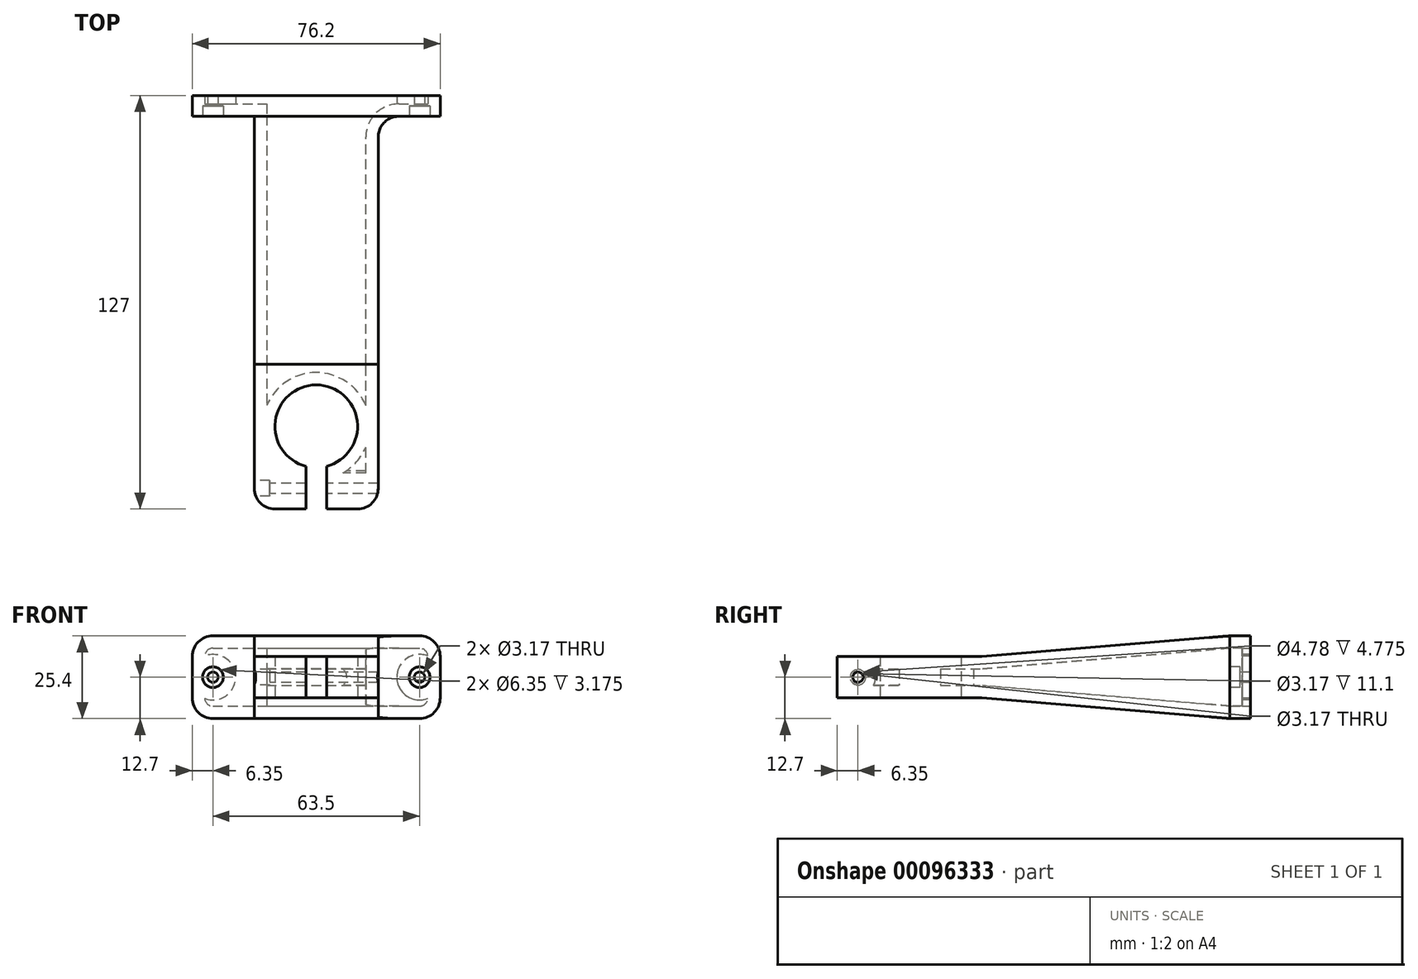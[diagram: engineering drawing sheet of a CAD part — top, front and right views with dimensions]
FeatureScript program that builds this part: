
annotation { "Feature Type Name" : "Feature", "Feature Type Description" : "" }
export const myFeature = defineFeature(function(context is Context, id is Id, definition is map)
    precondition{}
    {
        {
            var Q0;
            Q0=qCreatedBy(makeId("Front.planeOp"),FACE);
            var sketch = newSketch(context, id + "F0", { "sketchPlane" : qUnion([Q0])});
            skLineSegment(sketch, "E0.bottom", {"start": v(0, 0) * mm, "end": v(76.2, 0) * mm});
            skLineSegment(sketch, "E0.top", {"start": v(0, 25.4) * mm, "end": v(76.2, 25.4) * mm});
            skLineSegment(sketch, "E0.left", {"start": v(0, 0) * mm, "end": v(0, 25.4) * mm});
            skLineSegment(sketch, "E0.right", {"start": v(76.2, 0) * mm, "end": v(76.2, 25.4) * mm});
            skSolve(sketch);
        }
        {
            var Q0;
            Q0=makeQuery(id+"F0.imprint","IMPRINT",FACE,{"disambiguationData":[TD([[makeQuery(id+"F0.imprint","IMPRINT",EDGE,{"derivedFrom":sQuery(id+"F0.wireOp",EDGE,"E0.bottom")}),1.0]])]});
            extrude(context, id + "F1", {"entities" : qUnion([Q0]), "depth" : 6.35 * mm});
        }
        {
            var Q0;
            Q0=makeQuery(id+"F1.opExtrude","CAP_FACE",FACE,{"disambiguationData":[OSD([sQuery(id+"F0.wireOp",EDGE,"E0.bottom"),sQuery(id+"F0.wireOp",EDGE,"E0.top"),sQuery(id+"F0.wireOp",EDGE,"E0.left"),sQuery(id+"F0.wireOp",EDGE,"E0.right")])],"isStart":false});
            var sketch = newSketch(context, id + "F2", { "sketchPlane" : qUnion([Q0])});
            skPoint(sketch, "E1", {"position": v(6.35, 12.7) * mm});
            skPoint(sketch, "E1.positionSnap0", {"position": v(0, 12.7) * mm});
            skPoint(sketch, "E2", {"position": v(76.2, 12.7) * mm});
            skPoint(sketch, "E3", {"position": v(69.85, 12.7) * mm});
            skSolve(sketch);
        }
        {
            var Q0;
            Q0=sQuery(id+"F2.wireOp",VERTEX,"E1");
            var Q1;
            Q1=sQuery(id+"F2.wireOp",VERTEX,"E3");
            var Q2;
            Q2=makeQuery(id+"F1.opExtrude","SWEPT_BODY",BODY,{"disambiguationData":[OSD([sQuery(id+"F0.wireOp",EDGE,"E0.bottom"),sQuery(id+"F0.wireOp",EDGE,"E0.top"),sQuery(id+"F0.wireOp",EDGE,"E0.left"),sQuery(id+"F0.wireOp",EDGE,"E0.right")])]});
            hole(context, id + "F3", {"style" : HoleStyle.C_BORE, "endStyle" : HoleEndStyle.THROUGH, "holeDiameter" : 3.17 * mm, "cBoreDiameter" : 6.35 * mm, "cBoreDepth" : 3.17 * mm, "locations" : qUnion([Q0, Q1]), "scope" : qUnion([Q2]), "isTappedThrough" : true});
        }
        {
            var Q0;
            Q0=makeQuery(id+"F1.opExtrude","CAP_FACE",FACE,{"disambiguationData":[OSD([sQuery(id+"F0.wireOp",EDGE,"E0.bottom"),sQuery(id+"F0.wireOp",EDGE,"E0.top"),sQuery(id+"F0.wireOp",EDGE,"E0.left"),sQuery(id+"F0.wireOp",EDGE,"E0.right")])],"isStart":false});
            var sketch = newSketch(context, id + "F4", { "sketchPlane" : qUnion([Q0])});
            skLineSegment(sketch, "E4.bottom", {"start": v(19.05, 25.4) * mm, "end": v(57.15, 25.4) * mm});
            skLineSegment(sketch, "E4.top", {"start": v(19.05, 0) * mm, "end": v(57.15, 0) * mm});
            skLineSegment(sketch, "E4.left", {"start": v(19.05, 25.4) * mm, "end": v(19.05, 0) * mm});
            skLineSegment(sketch, "E4.right", {"start": v(57.15, 25.4) * mm, "end": v(57.15, 0) * mm});
            skSolve(sketch);
        }
        {
            var Q0;
            Q0=makeQuery(id+"F4.imprint","IMPRINT",FACE,{"disambiguationData":[TD([[makeQuery(id+"F4.imprint","IMPRINT",EDGE,{"derivedFrom":sQuery(id+"F4.wireOp",EDGE,"E4.bottom")}),-1.0]])]});
            cPlane(context, id + "F5", {"entities" : qUnion([Q0]), "cplaneType" : CPlaneType.OFFSET, "offset" : 76.2 * mm, "width" : 152.4 * mm, "height" : 152.4 * mm});
        }
        {
            var Q0;
            Q0=qCreatedBy(id+"F5.planeOp",FACE);
            var sketch = newSketch(context, id + "F6", { "sketchPlane" : qUnion([Q0])});
            skLineSegment(sketch, "E5.0", {"start": v(19.05, 25.4) * mm, "end": v(57.15, 25.4) * mm, "construction": true});
            skLineSegment(sketch, "E6.0", {"start": v(19.05, 0) * mm, "end": v(57.15, 0) * mm, "construction": true});
            skLineSegment(sketch, "E7.0", {"start": v(19.05, 25.4) * mm, "end": v(19.05, 0) * mm, "construction": true});
            skLineSegment(sketch, "E8.0", {"start": v(57.15, 25.4) * mm, "end": v(57.15, 0) * mm, "construction": true});
            skLineSegment(sketch, "E9.bottom", {"start": v(19.05, 19.05) * mm, "end": v(57.15, 19.05) * mm});
            skLineSegment(sketch, "E9.top", {"start": v(19.05, 6.35) * mm, "end": v(57.15, 6.35) * mm});
            skLineSegment(sketch, "E9.left", {"start": v(19.05, 19.05) * mm, "end": v(19.05, 6.35) * mm});
            skLineSegment(sketch, "E9.right", {"start": v(57.15, 19.05) * mm, "end": v(57.15, 6.35) * mm});
            skSolve(sketch);
        }
        {
            var Q1;
            Q1=makeQuery(id+"F6.imprint","IMPRINT",FACE,{"disambiguationData":[TD([[makeQuery(id+"F6.imprint","IMPRINT",EDGE,{"derivedFrom":sQuery(id+"F6.wireOp",EDGE,"E9.bottom")}),-1.0]])]});
            var Q2;
            Q2=makeQuery(id+"F4.imprint","IMPRINT",FACE,{"disambiguationData":[TD([[makeQuery(id+"F4.imprint","IMPRINT",EDGE,{"derivedFrom":sQuery(id+"F4.wireOp",EDGE,"E4.bottom")}),-1.0]])]});
            loft(context, id + "F7", {"operationType" : NewBodyOperationType.ADD, "sheetProfilesArray" : [{ "sheetProfileEntities" : qUnion([Q1]) }, { "sheetProfileEntities" : qUnion([Q2]) }]});
        }
        {
            var Q0;
            Q0=makeQuery(id+"F7.opLoft","CAP_FACE",FACE,{"disambiguationData":[OSD([makeQuery(id+"F6.imprint","IMPRINT",FACE,{"disambiguationData":[TD([[makeQuery(id+"F6.imprint","IMPRINT",EDGE,{"derivedFrom":sQuery(id+"F6.wireOp",EDGE,"E9.bottom")}),-1.0]])]})])],"isStart":true});
            extrude(context, id + "F8", {"entities" : qUnion([Q0]), "operationType" : NewBodyOperationType.ADD, "depth" : 38.1 * mm});
        }
        {
            var Q0;
            Q0=makeQuery(id+"F8.opExtrude","SWEPT_FACE",FACE,{"disambiguationData":[OSD([sQuery(id+"F6.wireOp",EDGE,"E9.top"),sQuery(id+"F6.wireOp",EDGE,"E9.left"),sQuery(id+"F6.wireOp",EDGE,"E9.right")])]});
            var sketch = newSketch(context, id + "F9", { "sketchPlane" : qUnion([Q0])});
            skPoint(sketch, "E10", {"position": v(38.1, 101.6) * mm});
            skPoint(sketch, "E10.positionSnap0", {"position": v(57.15, 101.6) * mm});
            skPoint(sketch, "E10.positionSnap1", {"position": v(38.1, 120.65) * mm});
            skSolve(sketch);
        }
        {
            var Q0;
            Q0=sQuery(id+"F9.wireOp",VERTEX,"E10");
            var Q1;
            Q1=makeQuery(id+"F1.opExtrude","SWEPT_BODY",BODY,{"disambiguationData":[OSD([sQuery(id+"F0.wireOp",EDGE,"E0.bottom"),sQuery(id+"F0.wireOp",EDGE,"E0.top"),sQuery(id+"F0.wireOp",EDGE,"E0.left"),sQuery(id+"F0.wireOp",EDGE,"E0.right")])]});
            hole(context, id + "F10", {"style" : HoleStyle.SIMPLE, "endStyle" : HoleEndStyle.THROUGH, "holeDiameter" : 25.4 * mm, "locations" : qUnion([Q0]), "scope" : qUnion([Q1]), "isTappedThrough" : true});
        }
        {
            var Q0;
            Q0=makeQuery(id+"F8.opExtrude","SWEPT_FACE",FACE,{"disambiguationData":[OSD([sQuery(id+"F6.wireOp",EDGE,"E9.top"),sQuery(id+"F6.wireOp",EDGE,"E9.left"),sQuery(id+"F6.wireOp",EDGE,"E9.right")])]});
            var sketch = newSketch(context, id + "F11", { "sketchPlane" : qUnion([Q0])});
            skLineSegment(sketch, "E11", {"start": v(34.92, 120.65) * mm, "end": v(34.92, 113.9) * mm});
            skLineSegment(sketch, "E12", {"start": v(41.28, 120.65) * mm, "end": v(41.28, 113.9) * mm});
            skSolve(sketch);
        }
        {
            var Q0;
            {var subQ0=sQuery(id+"F11.wireOp",EDGE,"E11");Q0=makeQuery(id+"F11.imprint","IMPRINT",FACE,{"disambiguationData":[TD([[makeQuery(id+"F11.imprint","IMPRINT",EDGE,{"derivedFrom":subQ0}),1.0]])]});}
            extrude(context, id + "F12", {"entities" : qUnion([Q0]), "operationType" : NewBodyOperationType.REMOVE, "endBound" : BoundingType.THROUGH_ALL, "oppositeDirection" : true, "depth" : 25.4 * mm});
        }
        {
            var Q0;
            {var subQ3=sQuery(id+"F6.wireOp",EDGE,"E9.bottom");Q0=makeQuery(id+"F12.boolean.opBoolean","SPLIT",FACE,{"disambiguationData":[TD([makeQuery(id+"F12.opExtrude","SWEPT_FACE",FACE,{"disambiguationData":[OSD([sQuery(id+"F11.wireOp",EDGE,"E11")])]})])],"derivedFrom":makeQuery(id+"F8.opExtrude","CAP_FACE",FACE,{"disambiguationData":[OSD([makeQuery(id+"F6.imprint","IMPRINT",FACE,{"disambiguationData":[TD([[makeQuery(id+"F6.imprint","IMPRINT",EDGE,{"derivedFrom":subQ3}),-1.0]])]})])],"isStart":false})});}
            extrude(context, id + "F13", {"entities" : qUnion([Q0]), "operationType" : NewBodyOperationType.ADD, "depth" : 6.35 * mm});
        }
        {
            var Q0;
            {var subQ2=sQuery(id+"F6.wireOp",EDGE,"E9.bottom");Q0=makeQuery(id+"F12.boolean.opBoolean","SPLIT",FACE,{"disambiguationData":[TD([makeQuery(id+"F12.opExtrude","SWEPT_FACE",FACE,{"disambiguationData":[OSD([sQuery(id+"F11.wireOp",EDGE,"E12")])]})])],"derivedFrom":makeQuery(id+"F8.opExtrude","CAP_FACE",FACE,{"disambiguationData":[OSD([makeQuery(id+"F6.imprint","IMPRINT",FACE,{"disambiguationData":[TD([[makeQuery(id+"F6.imprint","IMPRINT",EDGE,{"derivedFrom":subQ2}),-1.0]])]})])],"isStart":false})});}
            extrude(context, id + "F14", {"entities" : qUnion([Q0]), "operationType" : NewBodyOperationType.ADD, "depth" : 6.35 * mm});
        }
        {
            var Q0;
            {var subQ0=sQuery(id+"F6.wireOp",EDGE,"E9.left");var subQ1=sQuery(id+"F6.wireOp",EDGE,"E9.top");var subQ2=sQuery(id+"F6.wireOp",EDGE,"E9.bottom");Q0=makeQuery(id+"F13.boolean.opBoolean","MERGE",FACE,{"derivedFrom":[makeQuery(id+"F8.boolean.opBoolean","MERGE",FACE,{"derivedFrom":[makeQuery(id+"F7.opLoft","SWEPT_FACE",FACE,{"disambiguationData":[OSD([sQuery(id+"F0.wireOp",EDGE,"E0.bottom"),sQuery(id+"F0.wireOp",EDGE,"E0.top"),sQuery(id+"F4.wireOp",EDGE,"E4.bottom"),sQuery(id+"F4.wireOp",EDGE,"E4.top"),sQuery(id+"F4.wireOp",EDGE,"E4.left"),subQ2,subQ1,subQ0])]}),makeQuery(id+"F8.opExtrude","SWEPT_FACE",FACE,{"disambiguationData":[OSD([subQ2,subQ1,subQ0])]})]}),makeQuery(id+"F13.opExtrude","SWEPT_FACE",FACE,{"disambiguationData":[OSD([subQ2,subQ1,subQ0])]})]});}
            var sketch = newSketch(context, id + "F15", { "sketchPlane" : qUnion([Q0])});
            skPoint(sketch, "E13", {"position": v(120.65, 12.7) * mm});
            skPoint(sketch, "E13.positionSnap0", {"position": v(127, 12.7) * mm});
            skSolve(sketch);
        }
        {
            var Q0;
            Q0=sQuery(id+"F15.wireOp",VERTEX,"E13");
            var Q1;
            Q1=makeQuery(id+"F1.opExtrude","SWEPT_BODY",BODY,{"disambiguationData":[OSD([sQuery(id+"F0.wireOp",EDGE,"E0.bottom"),sQuery(id+"F0.wireOp",EDGE,"E0.top"),sQuery(id+"F0.wireOp",EDGE,"E0.left"),sQuery(id+"F0.wireOp",EDGE,"E0.right")])]});
            hole(context, id + "F16", {"style" : HoleStyle.C_BORE, "endStyle" : HoleEndStyle.THROUGH, "holeDiameter" : 3.17 * mm, "cBoreDiameter" : 4.78 * mm, "cBoreDepth" : 4.78 * mm, "locations" : qUnion([Q0]), "scope" : qUnion([Q1]), "isTappedThrough" : true});
        }
        {
            var Q0;
            Q0=makeQuery(id+"F1.opExtrude","SWEPT_EDGE",EDGE,{"disambiguationData":[OSD([sQuery(id+"F0.wireOp",EDGE,"E0.bottom"),sQuery(id+"F0.wireOp",EDGE,"E0.left")])]});
            var Q1;
            Q1=makeQuery(id+"F7.opLoft","MID_CAP_EDGE",EDGE,{"disambiguationData":[OSD([sQuery(id+"F0.wireOp",EDGE,"E0.bottom"),sQuery(id+"F0.wireOp",EDGE,"E0.top"),sQuery(id+"F4.wireOp",EDGE,"E4.bottom"),sQuery(id+"F4.wireOp",EDGE,"E4.top"),sQuery(id+"F4.wireOp",EDGE,"E4.left")])],"capPos":1.0});
            var Q2;
            Q2=makeQuery(id+"F1.opExtrude","SWEPT_EDGE",EDGE,{"disambiguationData":[OSD([sQuery(id+"F0.wireOp",EDGE,"E0.top"),sQuery(id+"F0.wireOp",EDGE,"E0.left")])]});
            var Q3;
            Q3=makeQuery(id+"F1.opExtrude","SWEPT_EDGE",EDGE,{"disambiguationData":[OSD([sQuery(id+"F0.wireOp",EDGE,"E0.bottom"),sQuery(id+"F0.wireOp",EDGE,"E0.right")])]});
            var Q4;
            Q4=makeQuery(id+"F1.opExtrude","SWEPT_EDGE",EDGE,{"disambiguationData":[OSD([sQuery(id+"F0.wireOp",EDGE,"E0.top"),sQuery(id+"F0.wireOp",EDGE,"E0.right")])]});
            var Q5;
            Q5=makeQuery(id+"F7.opLoft","MID_CAP_EDGE",EDGE,{"disambiguationData":[OSD([sQuery(id+"F0.wireOp",EDGE,"E0.bottom"),sQuery(id+"F0.wireOp",EDGE,"E0.top"),sQuery(id+"F4.wireOp",EDGE,"E4.bottom"),sQuery(id+"F4.wireOp",EDGE,"E4.top"),sQuery(id+"F4.wireOp",EDGE,"E4.right")])],"capPos":1.0});
            var Q6;
            Q6=makeQuery(id+"F13.opExtrude","CAP_EDGE",EDGE,{"disambiguationData":[OSD([sQuery(id+"F6.wireOp",EDGE,"E9.bottom"),sQuery(id+"F6.wireOp",EDGE,"E9.top"),sQuery(id+"F6.wireOp",EDGE,"E9.left")])],"isStart":false});
            var Q7;
            Q7=makeQuery(id+"F14.opExtrude","CAP_EDGE",EDGE,{"disambiguationData":[OSD([sQuery(id+"F6.wireOp",EDGE,"E9.bottom"),sQuery(id+"F6.wireOp",EDGE,"E9.top"),sQuery(id+"F6.wireOp",EDGE,"E9.right")])],"isStart":false});
            fillet(context, id + "F17", {"entities" : qUnion([Q0, Q1, Q2, Q3, Q4, Q5, Q6, Q7]), "radius" : 6.35 * mm, "tangentPropagation" : true, "allowEdgeOverflow" : false});
        }
        {
            var Q0;
            Q0=makeQuery(id+"F1.opExtrude","CAP_FACE",FACE,{"disambiguationData":[OSD([sQuery(id+"F0.wireOp",EDGE,"E0.bottom"),sQuery(id+"F0.wireOp",EDGE,"E0.top"),sQuery(id+"F0.wireOp",EDGE,"E0.left"),sQuery(id+"F0.wireOp",EDGE,"E0.right")])],"isStart":true});
            shell(context, id + "F18", {"entities" : qUnion([Q0]), "thickness" : 3.8 * mm});
        }
    });
